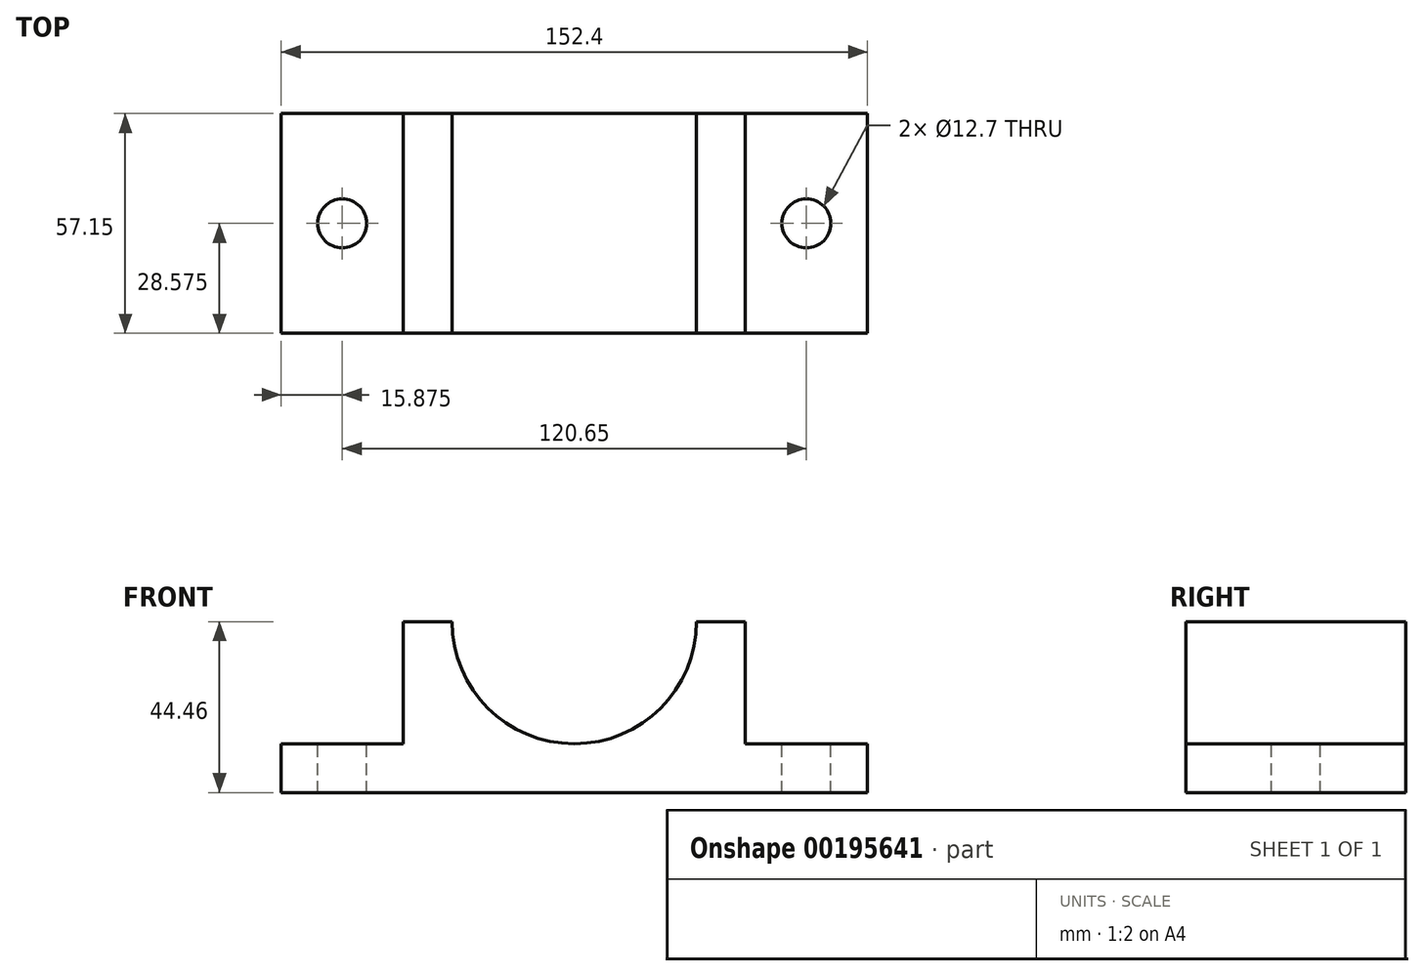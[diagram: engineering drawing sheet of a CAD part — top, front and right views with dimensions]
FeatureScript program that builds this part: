
annotation { "Feature Type Name" : "Feature", "Feature Type Description" : "" }
export const myFeature = defineFeature(function(context is Context, id is Id, definition is map)
    precondition{}
    {
        {
            var Q0;
            Q0=qCreatedBy(makeId("Front.planeOp"),FACE);
            var sketch = newSketch(context, id + "F0", { "sketchPlane" : qUnion([Q0])});
            skLineSegment(sketch, "E0.bottom", {"start": v(76.2, -22.22) * mm, "end": v(-76.2, -22.23) * mm});
            skLineSegment(sketch, "E0.top", {"start": v(44.45, 22.23) * mm, "end": v(31.75, 22.23) * mm});
            skLineSegment(sketch, "E0.left", {"start": v(76.2, -22.22) * mm, "end": v(76.2, -9.52) * mm});
            skLineSegment(sketch, "E0.right", {"start": v(-76.2, -22.23) * mm, "end": v(-76.2, -9.53) * mm});
            skPoint(sketch, "E0.middle", {"position": v(0, 0) * mm});
            skLineSegment(sketch, "E1", {"start": v(-76.2, -9.53) * mm, "end": v(-44.45, -9.53) * mm});
            skLineSegment(sketch, "E2", {"start": v(-44.45, -9.53) * mm, "end": v(-44.45, 22.22) * mm});
            skLineSegment(sketch, "E3.MirrorCS", {"start": v(76.2, -9.52) * mm, "end": v(44.45, -9.52) * mm});
            skLineSegment(sketch, "E4.MirrorCS", {"start": v(44.45, -9.52) * mm, "end": v(44.45, 22.23) * mm});
            skPoint(sketch, "E5.orphan", {"position": v(76.2, 22.23) * mm});
            skPoint(sketch, "E6.orphan", {"position": v(-76.2, 22.22) * mm});
            skLineSegment(sketch, "E7.MirrorCS", {"start": v(-44.45, 22.22) * mm, "end": v(-31.75, 22.22) * mm});
            skArc(sketch, "E8", {"start": v(-31.75, 22.22) * mm, "mid": v(0, -9.52) * mm, "end": v(31.75, 22.23) * mm});
            skPoint(sketch, "E9.end.orphan", {"position": v(0, -22.23) * mm});
            skSolve(sketch);
        }
        {
            var Q0;
            Q0=makeQuery(id+"F0.imprint","IMPRINT",FACE,{"disambiguationData":[TD([[makeQuery(id+"F0.imprint","IMPRINT",EDGE,{"derivedFrom":sQuery(id+"F0.wireOp",EDGE,"E0.bottom")}),-1.0]])]});
            extrude(context, id + "F1", {"entities" : qUnion([Q0]), "depth" : 57.15 * mm});
        }
        {
            var Q0;
            Q0=makeQuery(id+"F1.opExtrude","SWEPT_FACE",FACE,{"disambiguationData":[OSD([sQuery(id+"F0.wireOp",EDGE,"E3.MirrorCS")])]});
            var sketch = newSketch(context, id + "F2", { "sketchPlane" : qUnion([Q0])});
            skCircle(sketch, "E10", {"center": v(60.33, -28.58) * mm, "radius": 6.35 * mm});
            skPoint(sketch, "E10.centerSnap0", {"position": v(60.33, 0) * mm});
            skPoint(sketch, "E10.centerSnap1", {"position": v(76.2, -28.58) * mm});
            skSolve(sketch);
        }
        {
            var Q0;
            Q0=makeQuery(id+"F1.opExtrude","SWEPT_FACE",FACE,{"disambiguationData":[OSD([sQuery(id+"F0.wireOp",EDGE,"E1")])]});
            var sketch = newSketch(context, id + "F3", { "sketchPlane" : qUnion([Q0])});
            skCircle(sketch, "E11", {"center": v(-60.33, -28.58) * mm, "radius": 6.35 * mm});
            skPoint(sketch, "E12.orphan", {"position": v(-60.33, 0) * mm});
            skPoint(sketch, "E13.orphan", {"position": v(-44.45, -28.58) * mm});
            skPoint(sketch, "E14.start.orphan", {"position": v(-76.2, -28.58) * mm});
            skPoint(sketch, "E15.trimOffspring.end.orphan", {"position": v(-60.33, -57.15) * mm});
            skSolve(sketch);
        }
        {
            var Q0;
            Q0=makeQuery(id+"F3.imprint","IMPRINT",FACE,{"disambiguationData":[TD([[makeQuery(id+"F3.imprint","IMPRINT",EDGE,{"derivedFrom":sQuery(id+"F3.wireOp",EDGE,"E11")}),1.0]])]});
            var Q1;
            Q1=makeQuery(id+"F2.imprint","IMPRINT",FACE,{"disambiguationData":[TD([[makeQuery(id+"F2.imprint","IMPRINT",EDGE,{"derivedFrom":sQuery(id+"F2.wireOp",EDGE,"E10")}),1.0]])]});
            extrude(context, id + "F4", {"entities" : qUnion([Q0, Q1]), "operationType" : NewBodyOperationType.REMOVE, "oppositeDirection" : true, "depth" : 12.7 * mm});
        }
    });
